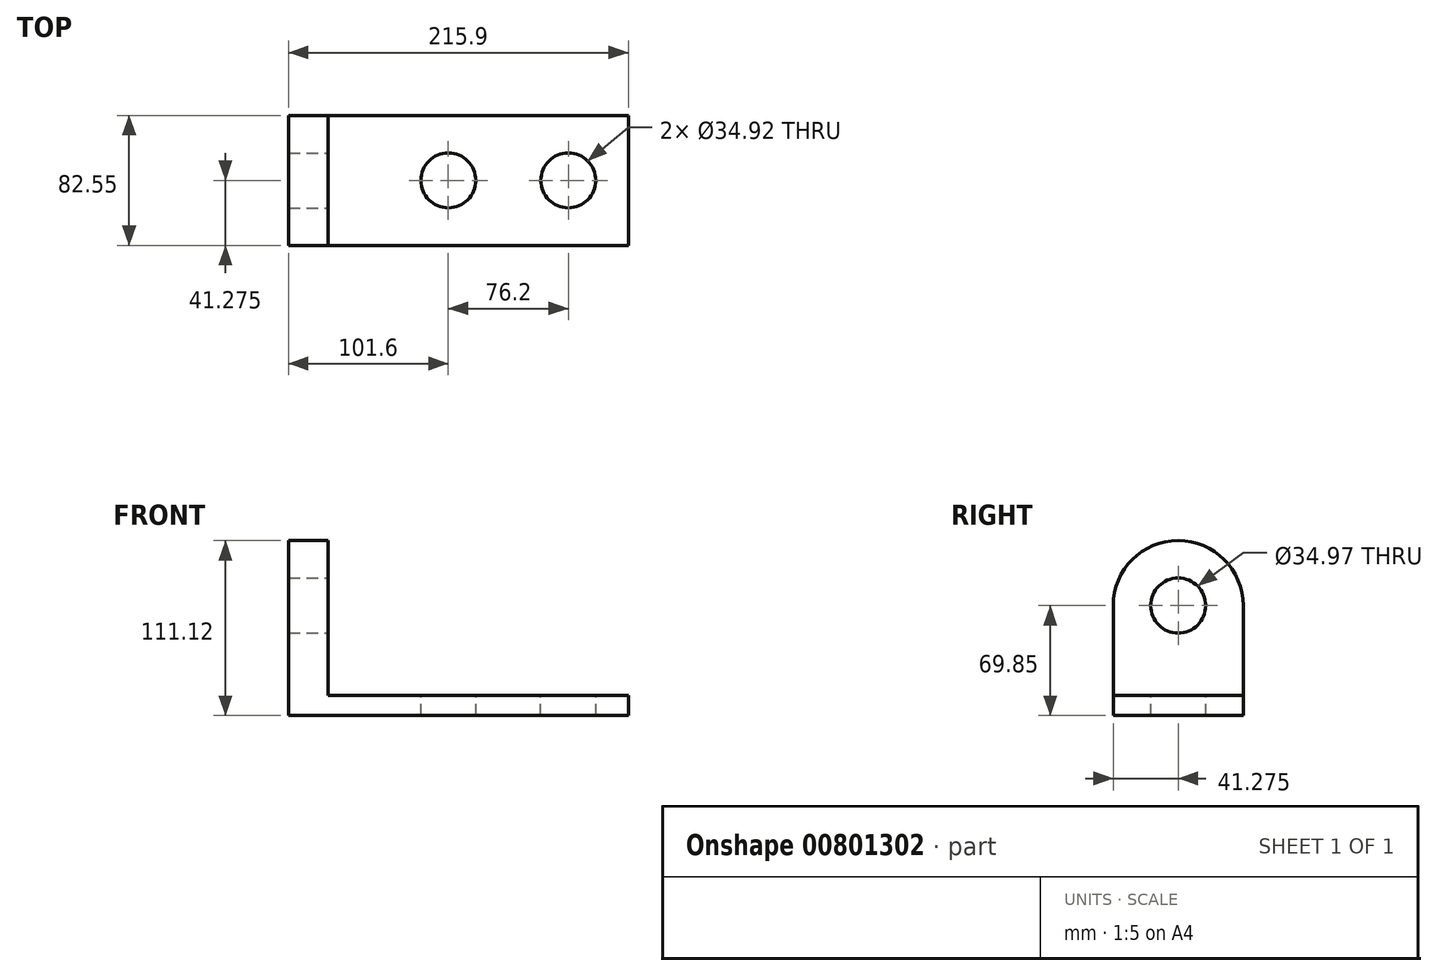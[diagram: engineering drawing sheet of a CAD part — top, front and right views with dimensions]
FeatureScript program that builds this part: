
annotation { "Feature Type Name" : "Feature", "Feature Type Description" : "" }
export const myFeature = defineFeature(function(context is Context, id is Id, definition is map)
    precondition{}
    {
        {
            var Q0;
            Q0=qCreatedBy(makeId("Front.planeOp"),FACE);
            var sketch = newSketch(context, id + "F0", { "sketchPlane" : qUnion([Q0])});
            skLineSegment(sketch, "E0", {"start": v(0, 0) * mm, "end": v(190.5, 0) * mm});
            skLineSegment(sketch, "E1", {"start": v(190.5, 0) * mm, "end": v(190.5, 12.7) * mm});
            skLineSegment(sketch, "E2", {"start": v(0, 0) * mm, "end": v(0, 12.7) * mm});
            skLineSegment(sketch, "E3", {"start": v(0, 12.7) * mm, "end": v(190.5, 12.7) * mm});
            skSolve(sketch);
        }
        {
            var Q0;
            Q0 = qSketchRegion(id + "F0", true);
            extrude(context, id + "F1", {"entities" : qUnion([Q0]), "depth" : 82.55 * mm, "offsetDistance" : 25.4 * mm});
        }
        {
            var Q0;
            Q0=makeQuery(id+"F1.opExtrude","CAP_FACE",FACE,{"disambiguationData":[OSD([sQuery(id+"F0.wireOp",EDGE,"E0"),sQuery(id+"F0.wireOp",EDGE,"E1"),sQuery(id+"F0.wireOp",EDGE,"E2"),sQuery(id+"F0.wireOp",EDGE,"E3")])],"isStart":false});
            var sketch = newSketch(context, id + "F2", { "sketchPlane" : qUnion([Q0])});
            skLineSegment(sketch, "E4", {"start": v(0, 0) * mm, "end": v(-25.4, 0) * mm});
            skLineSegment(sketch, "E5", {"start": v(-25.4, 0) * mm, "end": v(-25.4, 127) * mm});
            skLineSegment(sketch, "E6", {"start": v(0, 0) * mm, "end": v(0, 127) * mm});
            skLineSegment(sketch, "E7", {"start": v(-25.4, 127) * mm, "end": v(0, 127) * mm});
            skSolve(sketch);
        }
        {
            var Q0;
            Q0 = qSketchRegion(id + "F2", true);
            extrude(context, id + "F3", {"entities" : qUnion([Q0]), "operationType" : NewBodyOperationType.ADD, "oppositeDirection" : true, "depth" : 82.55 * mm, "offsetDistance" : 25.4 * mm});
        }
        {
            var Q0;
            Q0=makeQuery(id+"F3.opExtrude","SWEPT_FACE",FACE,{"disambiguationData":[OSD([sQuery(id+"F2.wireOp",EDGE,"E6")])]});
            var sketch = newSketch(context, id + "F4", { "sketchPlane" : qUnion([Q0])});
            skArc(sketch, "E8", {"start": v(0, 69.85) * mm, "mid": v(-41.28, 111.12) * mm, "end": v(-82.55, 69.85) * mm});
            skSolve(sketch);
        }
        {
            var Q0;
            Q0 = qSketchRegion(id + "F4", true);
            var Q1;
            {var subQ0=sQuery(id+"F4.wireOp",EDGE,"E8");Q1=makeQuery(id+"F4.imprint","IMPRINT",FACE,{"disambiguationData":[TD([[makeQuery(id+"F4.imprint","IMPRINT",EDGE,{"derivedFrom":subQ0}),-1.0]])]});}
            extrude(context, id + "F5", {"entities" : qUnion([Q0, Q1]), "operationType" : NewBodyOperationType.REMOVE, "endBound" : BoundingType.THROUGH_ALL, "oppositeDirection" : true, "depth" : 25.4 * mm, "offsetDistance" : 25.4 * mm});
        }
        {
            var Q0;
            Q0=makeQuery(id+"F3.opExtrude","SWEPT_FACE",FACE,{"disambiguationData":[OSD([sQuery(id+"F2.wireOp",EDGE,"E6")])]});
            var sketch = newSketch(context, id + "F6", { "sketchPlane" : qUnion([Q0])});
            skLineSegment(sketch, "E9", {"start": v(-41.28, 12.7) * mm, "end": v(-41.28, 69.85) * mm, "construction": true});
            skCircle(sketch, "E10", {"center": v(-41.28, 69.85) * mm, "radius": 17.49 * mm});
            skSolve(sketch);
        }
        {
            var Q0;
            Q0=makeQuery(id+"F6.imprint","IMPRINT",FACE,{"disambiguationData":[TD([[makeQuery(id+"F6.imprint","IMPRINT",EDGE,{"derivedFrom":sQuery(id+"F6.wireOp",EDGE,"E10")}),1.0]])]});
            extrude(context, id + "F7", {"entities" : qUnion([Q0]), "operationType" : NewBodyOperationType.REMOVE, "endBound" : BoundingType.THROUGH_ALL, "oppositeDirection" : true, "depth" : 25.4 * mm, "offsetDistance" : 25.4 * mm});
        }
        {
            var Q0;
            Q0=makeQuery(id+"F1.opExtrude","SWEPT_FACE",FACE,{"disambiguationData":[OSD([sQuery(id+"F0.wireOp",EDGE,"E3")])]});
            var sketch = newSketch(context, id + "F8", { "sketchPlane" : qUnion([Q0])});
            skLineSegment(sketch, "E11", {"start": v(190.5, -41.28) * mm, "end": v(152.4, -41.28) * mm, "construction": true});
            skLineSegment(sketch, "E12", {"start": v(152.4, -41.28) * mm, "end": v(76.2, -41.28) * mm, "construction": true});
            skCircle(sketch, "E13", {"center": v(76.2, -41.28) * mm, "radius": 17.46 * mm});
            skCircle(sketch, "E14", {"center": v(152.4, -41.28) * mm, "radius": 17.46 * mm});
            skSolve(sketch);
        }
        {
            var Q0;
            Q0=makeQuery(id+"F8.imprint","IMPRINT",FACE,{"disambiguationData":[TD([[makeQuery(id+"F8.imprint","IMPRINT",EDGE,{"derivedFrom":sQuery(id+"F8.wireOp",EDGE,"E13")}),1.0]])]});
            var Q1;
            Q1=makeQuery(id+"F8.imprint","IMPRINT",FACE,{"disambiguationData":[TD([[makeQuery(id+"F8.imprint","IMPRINT",EDGE,{"derivedFrom":sQuery(id+"F8.wireOp",EDGE,"E14")}),1.0]])]});
            extrude(context, id + "F9", {"entities" : qUnion([Q0, Q1]), "operationType" : NewBodyOperationType.REMOVE, "oppositeDirection" : true, "depth" : 25.4 * mm, "offsetDistance" : 25.4 * mm});
        }
    });
